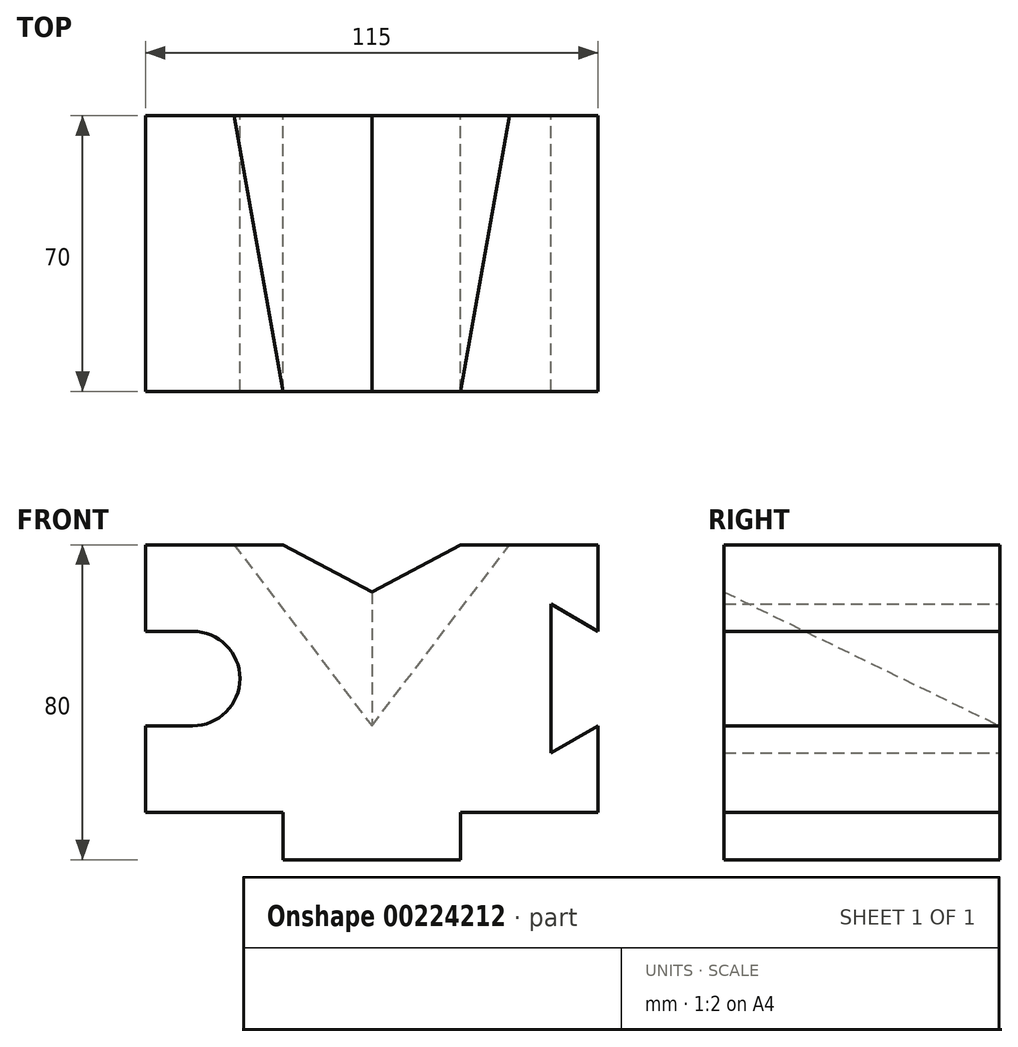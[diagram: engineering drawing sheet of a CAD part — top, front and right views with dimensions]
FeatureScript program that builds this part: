
annotation { "Feature Type Name" : "Feature", "Feature Type Description" : "" }
export const myFeature = defineFeature(function(context is Context, id is Id, definition is map)
    precondition{}
    {
        {
            var Q0;
            Q0=qCreatedBy(makeId("Front.planeOp"),FACE);
            var sketch = newSketch(context, id + "F0", { "sketchPlane" : qUnion([Q0])});
            skLineSegment(sketch, "E0", {"start": v(0, 0) * mm, "end": v(35, 0) * mm});
            skLineSegment(sketch, "E1", {"start": v(35, 0) * mm, "end": v(35, -12) * mm});
            skLineSegment(sketch, "E2", {"start": v(35, -12) * mm, "end": v(80, -12) * mm});
            skLineSegment(sketch, "E3", {"start": v(80, -12) * mm, "end": v(80, 0) * mm});
            skLineSegment(sketch, "E4", {"start": v(80, 0) * mm, "end": v(115, 0) * mm});
            skLineSegment(sketch, "E5", {"start": v(115, 0) * mm, "end": v(115, 22) * mm});
            skLineSegment(sketch, "E6", {"start": v(115, 22) * mm, "end": v(103, 15.07) * mm});
            skLineSegment(sketch, "E7", {"start": v(103, 15.07) * mm, "end": v(103, 52.93) * mm});
            skLineSegment(sketch, "E8", {"start": v(103, 52.93) * mm, "end": v(115, 46) * mm});
            skLineSegment(sketch, "E9", {"start": v(115, 46) * mm, "end": v(115, 68) * mm});
            skLineSegment(sketch, "E10", {"start": v(115, 68) * mm, "end": v(99.03, 68) * mm});
            skLineSegment(sketch, "E11", {"start": v(54.03, 68) * mm, "end": v(0, 68) * mm});
            skLineSegment(sketch, "E12", {"start": v(0, 68) * mm, "end": v(0, 46) * mm});
            skLineSegment(sketch, "E13", {"start": v(0, 0) * mm, "end": v(0, 22) * mm});
            skLineSegment(sketch, "E14", {"start": v(0, 22) * mm, "end": v(12, 22) * mm});
            skLineSegment(sketch, "E15", {"start": v(0, 46) * mm, "end": v(12, 46) * mm});
            skPoint(sketch, "E16.start.orphan", {"position": v(57.5, 56) * mm});
            skLineSegment(sketch, "E17", {"start": v(54.03, 68) * mm, "end": v(99.03, 68) * mm});
            skArc(sketch, "E18", {"start": v(12, 22) * mm, "mid": v(24, 34) * mm, "end": v(12, 46) * mm});
            skSolve(sketch);
        }
        {
            var Q0;
            Q0=makeQuery(id+"F0.imprint","IMPRINT",FACE,{"disambiguationData":[TD([[makeQuery(id+"F0.imprint","IMPRINT",EDGE,{"derivedFrom":sQuery(id+"F0.wireOp",EDGE,"E0")}),1.0]])]});
            extrude(context, id + "F1", {"entities" : qUnion([Q0]), "depth" : 70 * mm});
        }
        {
            var Q0;
            Q0=makeQuery(id+"F1.opExtrude","CAP_FACE",FACE,{"disambiguationData":[OSD([sQuery(id+"F0.wireOp",EDGE,"E0"),sQuery(id+"F0.wireOp",EDGE,"E1"),sQuery(id+"F0.wireOp",EDGE,"E2"),sQuery(id+"F0.wireOp",EDGE,"E3"),sQuery(id+"F0.wireOp",EDGE,"E4"),sQuery(id+"F0.wireOp",EDGE,"E5"),sQuery(id+"F0.wireOp",EDGE,"E6"),sQuery(id+"F0.wireOp",EDGE,"E7"),sQuery(id+"F0.wireOp",EDGE,"E8"),sQuery(id+"F0.wireOp",EDGE,"E9"),sQuery(id+"F0.wireOp",EDGE,"E10"),sQuery(id+"F0.wireOp",EDGE,"E11"),sQuery(id+"F0.wireOp",EDGE,"E12"),sQuery(id+"F0.wireOp",EDGE,"E13"),sQuery(id+"F0.wireOp",EDGE,"E14"),sQuery(id+"F0.wireOp",EDGE,"E15"),sQuery(id+"F0.wireOp",EDGE,"E17"),sQuery(id+"F0.wireOp",EDGE,"E18")])],"isStart":false});
            var sketch = newSketch(context, id + "F2", { "sketchPlane" : qUnion([Q0])});
            skLineSegment(sketch, "E19", {"start": v(35, 68) * mm, "end": v(80, 68) * mm});
            skLineSegment(sketch, "E20", {"start": v(80, 68) * mm, "end": v(57.5, 56) * mm});
            skLineSegment(sketch, "E21", {"start": v(57.5, 56) * mm, "end": v(35, 68) * mm});
            skSolve(sketch);
        }
        {
            var Q0;
            Q0=makeQuery(id+"F1.opExtrude","CAP_FACE",FACE,{"disambiguationData":[OSD([sQuery(id+"F0.wireOp",EDGE,"E0"),sQuery(id+"F0.wireOp",EDGE,"E1"),sQuery(id+"F0.wireOp",EDGE,"E2"),sQuery(id+"F0.wireOp",EDGE,"E3"),sQuery(id+"F0.wireOp",EDGE,"E4"),sQuery(id+"F0.wireOp",EDGE,"E5"),sQuery(id+"F0.wireOp",EDGE,"E6"),sQuery(id+"F0.wireOp",EDGE,"E7"),sQuery(id+"F0.wireOp",EDGE,"E8"),sQuery(id+"F0.wireOp",EDGE,"E9"),sQuery(id+"F0.wireOp",EDGE,"E10"),sQuery(id+"F0.wireOp",EDGE,"E11"),sQuery(id+"F0.wireOp",EDGE,"E12"),sQuery(id+"F0.wireOp",EDGE,"E13"),sQuery(id+"F0.wireOp",EDGE,"E14"),sQuery(id+"F0.wireOp",EDGE,"E15"),sQuery(id+"F0.wireOp",EDGE,"E17"),sQuery(id+"F0.wireOp",EDGE,"E18")])],"isStart":true});
            var sketch = newSketch(context, id + "F3", { "sketchPlane" : qUnion([Q0])});
            skLineSegment(sketch, "E22", {"start": v(-92.5, 68) * mm, "end": v(-22.5, 68) * mm});
            skLineSegment(sketch, "E23", {"start": v(-22.5, 68) * mm, "end": v(-57.5, 22) * mm});
            skLineSegment(sketch, "E24", {"start": v(-57.5, 22) * mm, "end": v(-92.5, 68) * mm});
            skSolve(sketch);
        }
        {
            var Q1;
            Q1 = qSketchRegion(id + "F2", true);
            var Q2;
            Q2 = qSketchRegion(id + "F3", true);
            loft(context, id + "F4", {"operationType" : NewBodyOperationType.REMOVE, "sheetProfilesArray" : [{ "sheetProfileEntities" : qUnion([Q1]) }, { "sheetProfileEntities" : qUnion([Q2]) }]});
        }
    });
